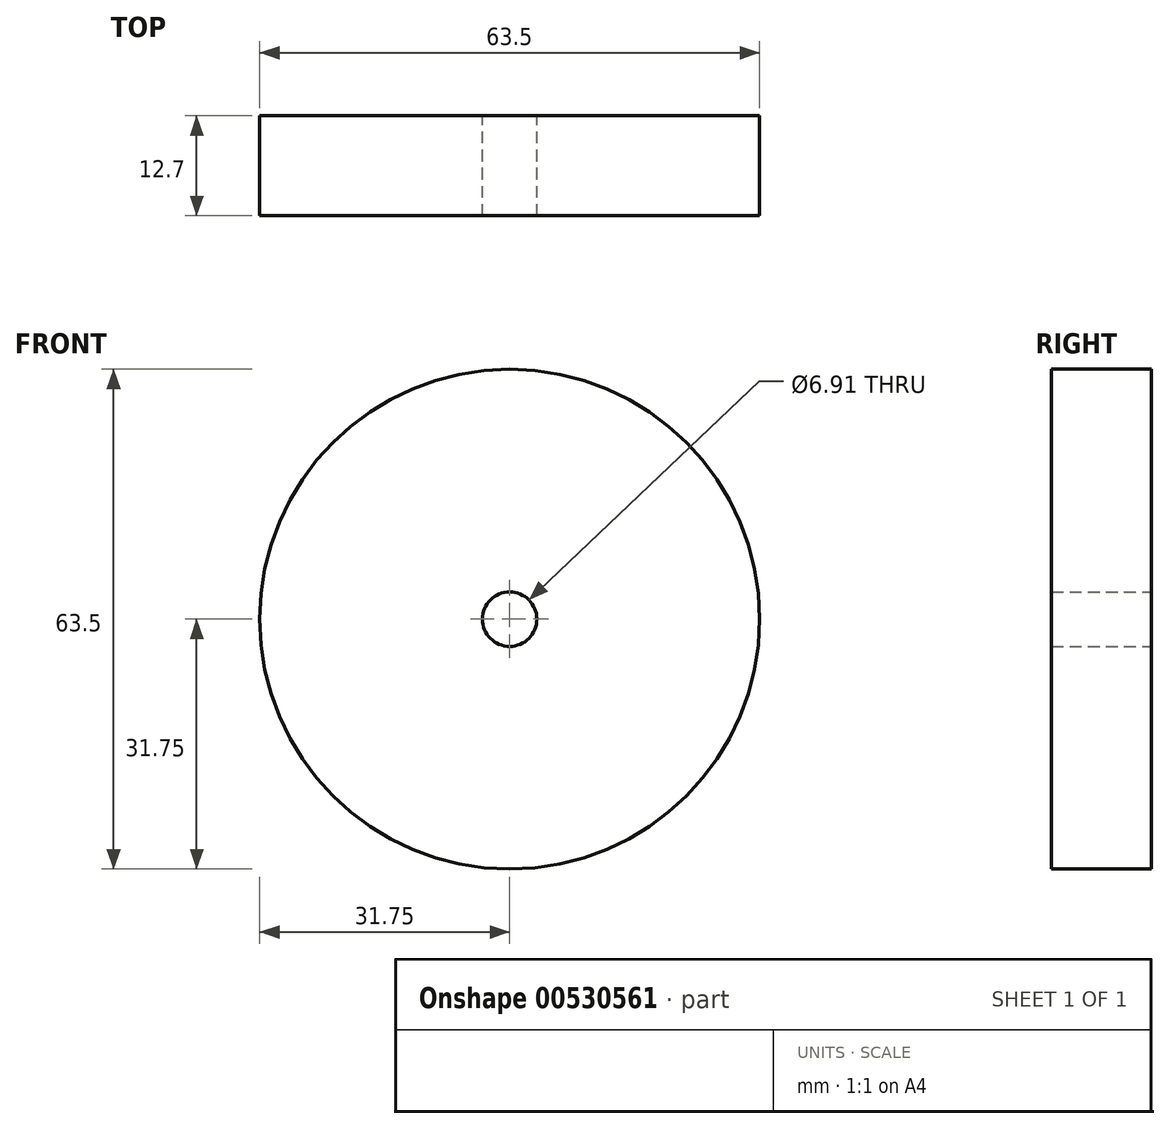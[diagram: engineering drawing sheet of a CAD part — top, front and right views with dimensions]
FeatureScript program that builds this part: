
annotation { "Feature Type Name" : "Feature", "Feature Type Description" : "" }
export const myFeature = defineFeature(function(context is Context, id is Id, definition is map)
    precondition{}
    {
        {
            var Q0;
            Q0=qCreatedBy(makeId("Front.planeOp"),FACE);
            var sketch = newSketch(context, id + "F0", { "sketchPlane" : qUnion([Q0])});
            skCircle(sketch, "E0", {"center": v(0, 0) * mm, "radius": 31.75 * mm});
            skCircle(sketch, "E1", {"center": v(0, 0) * mm, "radius": 3.45 * mm});
            skSolve(sketch);
        }
        {
            var Q0;
            Q0 = qSketchRegion(id + "F0", true);
            extrude(context, id + "F1", {"entities" : qUnion([Q0]), "depth" : 12.7 * mm, "offsetDistance" : 25.4 * mm});
        }
    });
